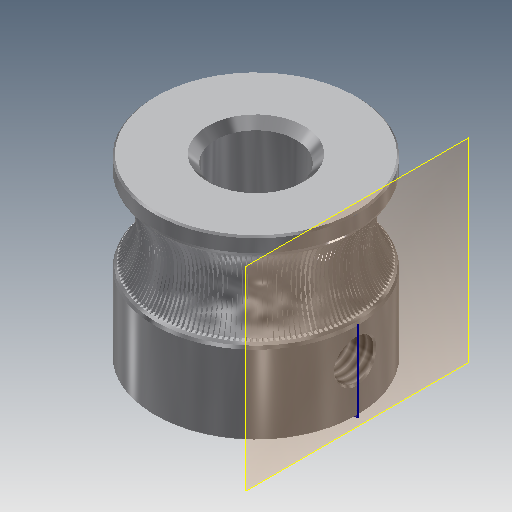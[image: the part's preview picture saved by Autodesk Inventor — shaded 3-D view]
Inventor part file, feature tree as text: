
AUTODESK INVENTOR PART (.ipt)
format: ipt  version: 2017 (Build 210142000, 142)  size: 3,525,120 bytes
history: native  units: mm
features: sketch x5, other x3, chamfer x3, hole x2, revolve x1, pattern_circular x1
ambient origin geometry x8: Origin, YZ Plane, XZ Plane, XY Plane, X Axis, Y Axis, Z Axis, Center Point
bodies: Body1 (feature_tree)
feature tree (15):
  other  "Bryła1"
  revolve  "Obrót1"
  chamfer  "Faza1"  Distance=6.3mm
  hole  "Otwór1"  [1 undecoded]
  chamfer  "Faza2"  Distance=5.0mm
  sketch  "Szkic4"
  other  "Płaszczyzna konstrukcyjna1"
  hole  "Otwór2"  [1 undecoded]
  chamfer  "Faza3"  Distance=5.3mm
  other  "Wypukłość2"
  pattern_circular  "Szyk kołowy3"  [2 undecoded]
  sketch  "Szkic1"
  sketch  "Szkic3"
  sketch  "Szkic5"
  sketch  "Szkic7"
note: 4 required parameter values undecoded (feature->parameter linkage not recoverable at this tier; creation-order binding heuristic only, values carry confidence <= 0.55)
